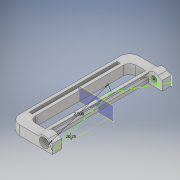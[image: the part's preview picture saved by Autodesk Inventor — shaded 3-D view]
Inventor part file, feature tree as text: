
AUTODESK INVENTOR PART (.ipt)
format: ipt  version: 2018 (Build 220112000, 112)  size: 234,496 bytes
history: native  units: in
note: dims shown in document units (in); Inventor stores cm internally (conversion verified against a paired STEP export)
features: sketch x16, extrude x9, fillet x6, hole x2, plane x1, mirror x1
ambient origin geometry x8: Origin, YZ Plane, XZ Plane, XY Plane, X Axis, Y Axis, Z Axis, Center Point
bodies: Solid1 (feature_tree)
feature tree (35):
  extrude  "Extrusion1"  Depth=0.375in
  sketch  "Sketch2"  dims[d3=0.375in d4=0.5in d5=0.375in d6=0.0in]
  extrude  "Extrusion2"  Depth=0.375in
  fillet  "Fillet1"  Radius=0.375in
  extrude  "Extrusion3"  Depth=0.375in
  extrude  "Extrusion4"  Depth=0.25in
  plane  "Work Plane1"
  mirror  "Mirror1"
  fillet  "Fillet2"  Radius=0.24in
  extrude  "Extrusion5"  Depth=0.375in
  sketch  "Sketch6"  dims[d17=1.0in d18=0.0in d19=0.24in d20=0.0in]
  extrude  "Extrusion6"  Depth=0.24in TaperAngle=0.0deg
  extrude  "Extrusion7"  Depth=0.375in
  fillet  "Fillet3"  Radius=0.25in
  fillet  "Fillet4"  Radius=0.375in
  fillet  "Fillet5"  Radius=0.25in
  fillet  "Fillet6"  Radius=0.125in
  sketch  "Sketch9"  dims[d30=0.125in d31=0.125in]
  extrude  "Extrusion8"  Depth=0.035in
  sketch  "Sketch11"  dims[d35=0.2in]
  sketch  "Sketch12"  dims[d36=0.2in d37=0.75in d38=0.375in d39=0.25in d40=0.5635in d41=0.35in d42=0.0in]
  hole  "Hole1"  [1 undecoded]
  hole  "Hole2"  [1 undecoded]
  sketch  "Sketch14"  dims[d51=3.5in]
  extrude  "Extrusion9"  Depth=0.125in
  sketch  "Sketch16"  dims[d54=2.5in d55=0.1391in]
  sketch  "Sketch1"  dims[d0=1.3in d1=0.375in]
  sketch  "Sketch3"  dims[d7=0.375in d8=0.0in d9=0.375in]
  sketch  "Sketch4"  dims[d10=0.24in d11=0.0in d12=0.25in d13=0.24in d14=0.0in]
  sketch  "Sketch5"  dims[d15=2.0in d16=0.375in]
  sketch  "Sketch7"  dims[d21=0.375in d22=0.0in d23=0.375in d24=0.25in d25=0.375in d26=0.25in d27=0.125in]
  sketch  "Sketch8"  dims[d28=0.035in d29=0.035in]
  sketch  "Sketch10"  dims[d32=4.375in d33=0.0in d34=0.2in]
  sketch  "Sketch13"  dims[d43=0.2in d44=0.75in d45=0.375in d46=0.25in d47=0.5635in d48=0.35in d49=0.0in d50=0.125in]
  sketch  "Sketch15"  dims[d52=0.375in d53=0.0in]
note: 2 required parameter values undecoded (feature->parameter linkage not recoverable at this tier; creation-order binding heuristic only, values carry confidence <= 0.55)
